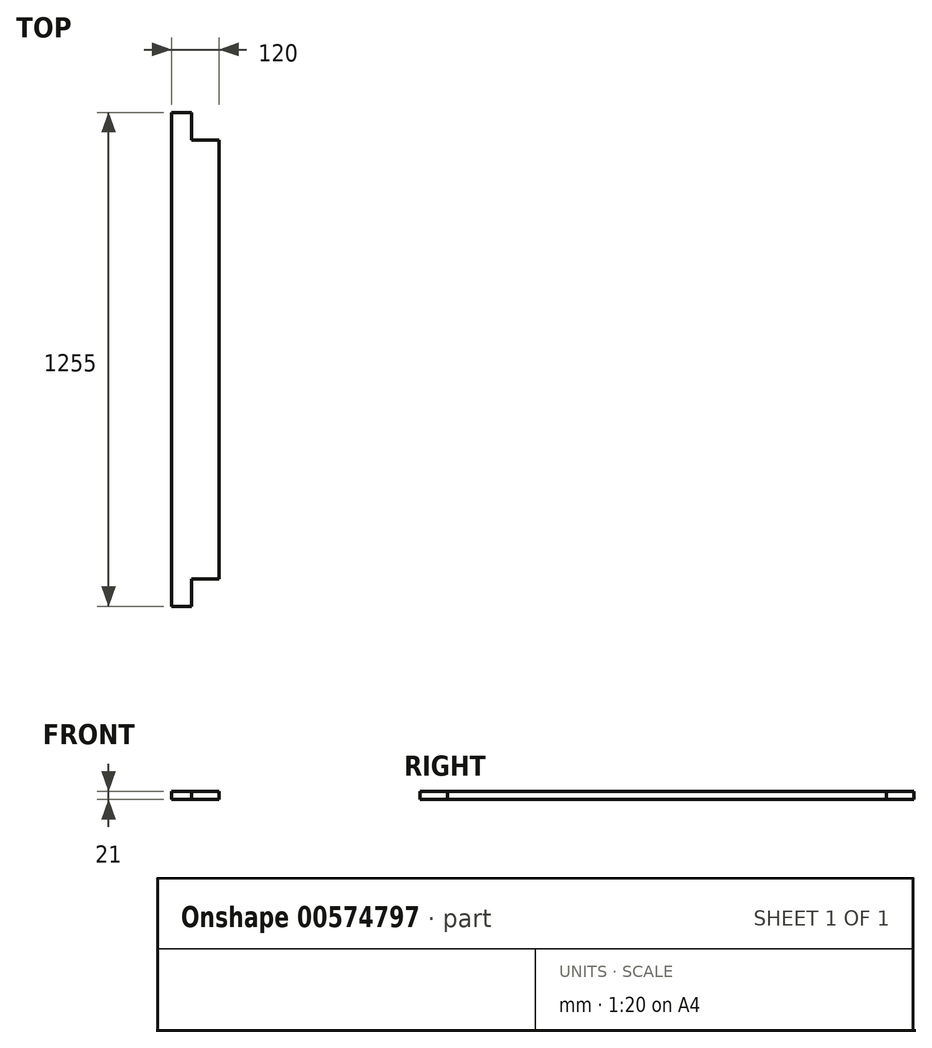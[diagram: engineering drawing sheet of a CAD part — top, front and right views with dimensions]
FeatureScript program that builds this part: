
annotation { "Feature Type Name" : "Feature", "Feature Type Description" : "" }
export const myFeature = defineFeature(function(context is Context, id is Id, definition is map)
    precondition{}
    {
        {
            var Q0;
            Q0=qCreatedBy(makeId("Front.planeOp"),FACE);
            var sketch = newSketch(context, id + "F0", { "sketchPlane" : qUnion([Q0])});
            skLineSegment(sketch, "E0.bottom", {"start": v(-60, -10.5) * mm, "end": v(60, -10.5) * mm});
            skLineSegment(sketch, "E0.top", {"start": v(-60, 10.5) * mm, "end": v(60, 10.5) * mm});
            skLineSegment(sketch, "E0.left", {"start": v(-60, -10.5) * mm, "end": v(-60, 10.5) * mm});
            skLineSegment(sketch, "E0.right", {"start": v(60, -10.5) * mm, "end": v(60, 10.5) * mm});
            skSolve(sketch);
        }
        {
            var Q0;
            Q0 = qSketchRegion(id + "F0", true);
            extrude(context, id + "F1", {"entities" : qUnion([Q0]), "depth" : 1255 * mm, "offsetDistance" : 25 * mm});
        }
        {
            var Q0;
            Q0=makeQuery(id+"F1.opExtrude","SWEPT_FACE",FACE,{"disambiguationData":[OSD([sQuery(id+"F0.wireOp",EDGE,"E0.top")])]});
            var sketch = newSketch(context, id + "F2", { "sketchPlane" : qUnion([Q0])});
            skLineSegment(sketch, "E1.bottom", {"start": v(60, -1255) * mm, "end": v(-10, -1255) * mm});
            skLineSegment(sketch, "E1.top", {"start": v(60, -1185) * mm, "end": v(-10, -1185) * mm});
            skLineSegment(sketch, "E1.left", {"start": v(60, -1255) * mm, "end": v(60, -1185) * mm});
            skLineSegment(sketch, "E1.right", {"start": v(-10, -1255) * mm, "end": v(-10, -1185) * mm});
            skLineSegment(sketch, "E2.bottom", {"start": v(60, 0) * mm, "end": v(-10, 0) * mm});
            skLineSegment(sketch, "E2.top", {"start": v(60, -70) * mm, "end": v(-10, -70) * mm});
            skLineSegment(sketch, "E2.left", {"start": v(60, 0) * mm, "end": v(60, -70) * mm});
            skLineSegment(sketch, "E2.right", {"start": v(-10, 0) * mm, "end": v(-10, -70) * mm});
            skSolve(sketch);
        }
        {
            var Q0;
            Q0=makeQuery(id+"F2.imprint","IMPRINT",FACE,{"disambiguationData":[TD([[makeQuery(id+"F2.imprint","IMPRINT",EDGE,{"derivedFrom":sQuery(id+"F2.wireOp",EDGE,"E1.bottom")}),1.0]])]});
            var Q1;
            Q1=makeQuery(id+"F2.imprint","IMPRINT",FACE,{"disambiguationData":[TD([[makeQuery(id+"F2.imprint","IMPRINT",EDGE,{"derivedFrom":sQuery(id+"F2.wireOp",EDGE,"E2.bottom")}),-1.0]])]});
            extrude(context, id + "F3", {"entities" : qUnion([Q0, Q1]), "operationType" : NewBodyOperationType.REMOVE, "oppositeDirection" : true, "depth" : 25 * mm, "offsetDistance" : 25 * mm});
        }
        {
            var Q0;
            Q0=makeQuery(id+"F1.opExtrude","SWEPT_BODY",BODY,{"disambiguationData":[OSD([sQuery(id+"F0.wireOp",EDGE,"E0.bottom"),sQuery(id+"F0.wireOp",EDGE,"E0.top"),sQuery(id+"F0.wireOp",EDGE,"E0.left"),sQuery(id+"F0.wireOp",EDGE,"E0.right")])]});
            transform(context, id + "F4", {"entities" : qUnion([Q0]), "transformType" : TransformType.TRANSLATION_3D, "dx" : 0 * mm, "dy" : 0 * mm, "dz" : 0 * mm, "makeCopy" : true});
        }
        {
            var Q0;
            Q0=makeQuery(id+"F1.opExtrude","SWEPT_BODY",BODY,{"disambiguationData":[OSD([sQuery(id+"F0.wireOp",EDGE,"E0.bottom"),sQuery(id+"F0.wireOp",EDGE,"E0.top"),sQuery(id+"F0.wireOp",EDGE,"E0.left"),sQuery(id+"F0.wireOp",EDGE,"E0.right")])]});
            deleteBodies(context, id + "F5", {"entities" : qUnion([Q0])});
        }
    });
